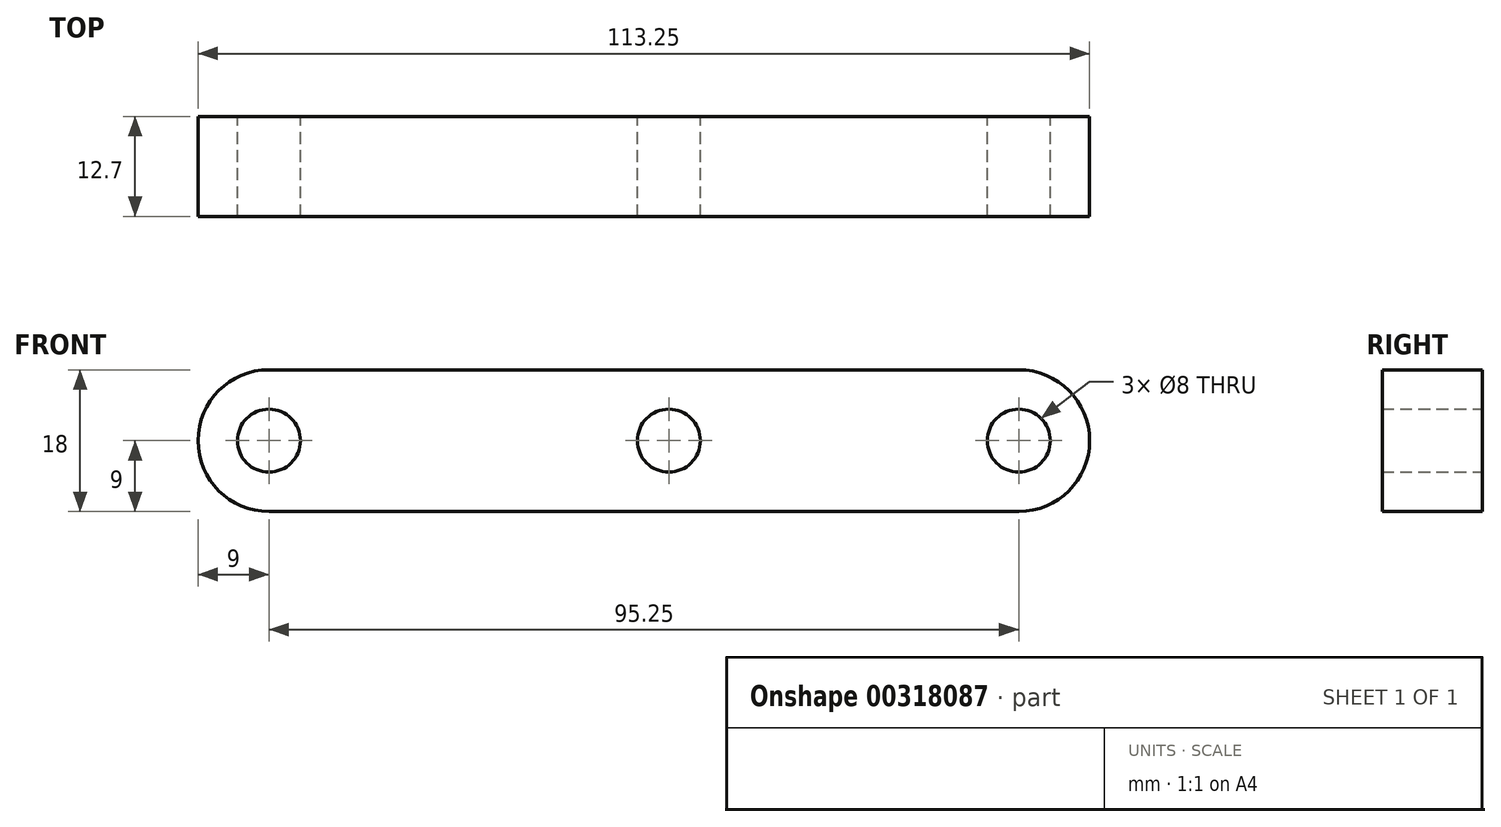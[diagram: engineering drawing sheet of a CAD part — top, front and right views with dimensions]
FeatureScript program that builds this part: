
annotation { "Feature Type Name" : "Feature", "Feature Type Description" : "" }
export const myFeature = defineFeature(function(context is Context, id is Id, definition is map)
    precondition{}
    {
        {
            var Q0;
            Q0=qCreatedBy(makeId("Front.planeOp"),FACE);
            var sketch = newSketch(context, id + "F0", { "sketchPlane" : qUnion([Q0])});
            skCircle(sketch, "E0.0", {"center": v(-50.8, 0) * mm, "radius": 4 * mm});
            skCircle(sketch, "E0.1", {"center": v(-50.8, 0) * mm, "radius": 9 * mm});
            skCircle(sketch, "E0.2", {"center": v(0, 0) * mm, "radius": 9 * mm});
            skCircle(sketch, "E0.4", {"center": v(0, 0) * mm, "radius": 4 * mm});
            skLineSegment(sketch, "E1", {"start": v(-50.8, -9) * mm, "end": v(0, -9) * mm});
            skCircle(sketch, "E2.2", {"center": v(44.45, 0) * mm, "radius": 9 * mm});
            skCircle(sketch, "E3.4", {"center": v(44.45, 0) * mm, "radius": 4 * mm});
            skLineSegment(sketch, "E4", {"start": v(-50.8, 9) * mm, "end": v(44.45, 9) * mm});
            skLineSegment(sketch, "E5", {"start": v(0, -9) * mm, "end": v(44.45, -9) * mm});
            skSolve(sketch);
        }
        {
            var Q0;
            {var subQ0=sQuery(id+"F0.wireOp",EDGE,"E0.3");Q0=makeQuery(id+"F0.imprint","IMPRINT",FACE,{"disambiguationData":[TD([[makeQuery(id+"F0.imprint","IMPRINT",EDGE,{"derivedFrom":subQ0}),-1.0]])]});}
            var Q1;
            Q1=makeQuery(id+"F0.imprint","IMPRINT",FACE,{"disambiguationData":[TD([[makeQuery(id+"F0.imprint","IMPRINT",EDGE,{"derivedFrom":sQuery(id+"F0.wireOp",EDGE,"E0.0")}),-1.0]])]});
            var Q2;
            {var subQ2=sQuery(id+"F0.wireOp",EDGE,"jpw7KzTM-zn4p-1V0Z-LJ1M-VFu4cGhIcsvI");Q2=makeQuery(id+"F0.imprint","IMPRINT",FACE,{"disambiguationData":[TD([[makeQuery(id+"F0.imprint","IMPRINT",EDGE,{"derivedFrom":subQ2}),1.0]])]});}
            var Q3;
            Q3=makeQuery(id+"F0.imprint","IMPRINT",FACE,{"disambiguationData":[TD([[makeQuery(id+"F0.imprint","IMPRINT",EDGE,{"derivedFrom":sQuery(id+"F0.wireOp",EDGE,"E0.4")}),-1.0]])]});
            var Q4;
            {var subQ0=sQuery(id+"F0.wireOp",EDGE,"E4");Q4=makeQuery(id+"F0.imprint","IMPRINT",FACE,{"disambiguationData":[TD([[makeQuery(id+"F0.imprint","IMPRINT",EDGE,{"derivedFrom":subQ0}),-1.0]])]});}
            var Q5;
            Q5=makeQuery(id+"F0.imprint","IMPRINT",FACE,{"disambiguationData":[TD([[makeQuery(id+"F0.imprint","IMPRINT",EDGE,{"derivedFrom":sQuery(id+"F0.wireOp",EDGE,"E3.4")}),-1.0]])]});
            extrude(context, id + "F1", {"entities" : qUnion([Q0, Q1, Q2, Q3, Q4, Q5]), "depth" : 12.7 * mm});
        }
    });
